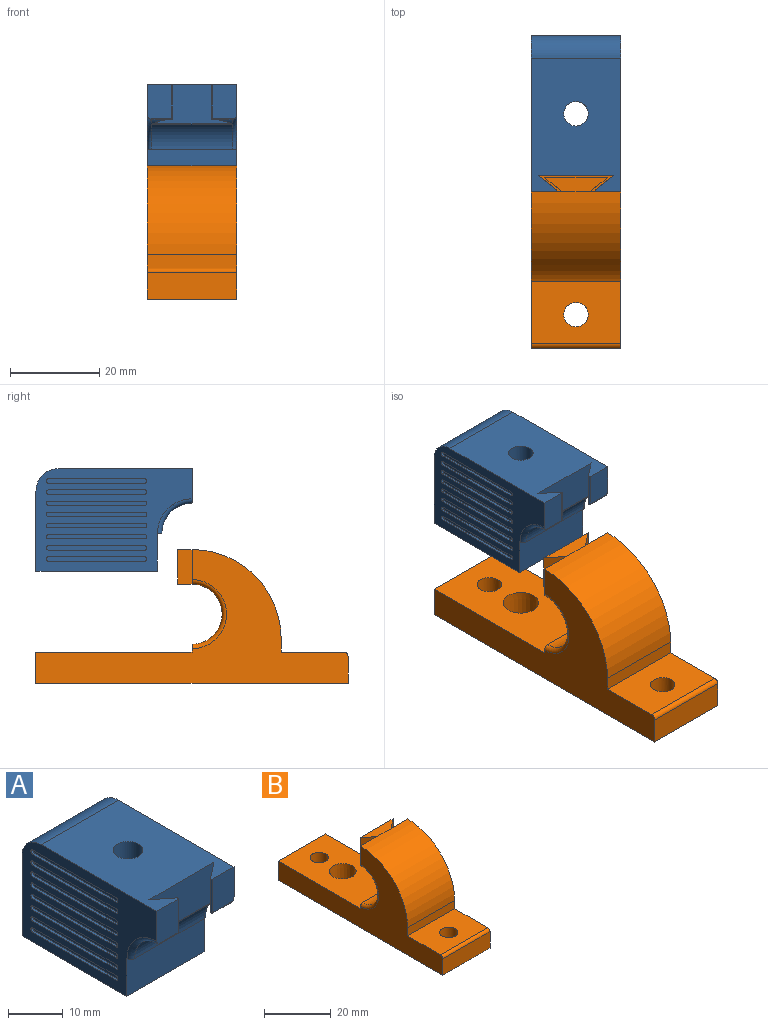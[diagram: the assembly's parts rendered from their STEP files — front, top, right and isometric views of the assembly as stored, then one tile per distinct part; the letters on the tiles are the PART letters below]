
ASSEMBLY  parts=2 mates=1
PART A: 114 faces, bbox 20.1x35.1x23.1 mm
  f0: cylinder r=6.75mm len=18mm, axis (1,0,0), area 119mm2, adj f5,f6,f15,f31
  f1: cylinder r=6.75mm len=4.48mm, axis (1,0,0), area 8.1mm2, adj f5,f24,f33
  f2: plane 7.5x5.48mm, normal (0,-1,0), area 41mm2, adj f4,f5,f7,f24,f25
  f3: cylinder r=6.75mm len=4.48mm, axis (1,0,0), area 8.1mm2, adj f6,f22,f26
  f4: plane 30x20mm, normal (0,0,1), area 531.4mm2, adj f2,f7,f10,f11,f16,f17,f18,f19
  f5: torus R=7.75mm, axis (-1,0,0), area 17.5mm2, adj f0,f1,f2,f7,f15,f24,f29,f32
  f6: torus R=7.75mm, axis (-1,0,0), area 17.5mm2, adj f0,f3,f10,f11,f15,f22,f27,f28
  f7: plane 35x23mm, normal (-1,0,0), area 507.5mm2, adj f2,f4,f5,f8,f9,f14,f15,f20
  f8: plane 27.22x20mm, normal (0,0,-1), area 407.5mm2, adj f7,f9,f10,f12,f14,f19
  f9: plane 20x18mm, normal (0,1,0), area 360mm2, adj f7,f8,f10,f20
  f10: plane 35x23mm, normal (1,0,0), area 507.5mm2, adj f4,f6,f8,f9,f11,f14,f15,f20
  f11: plane 7.5x5.48mm, normal (0,-1,0), area 41mm2, adj f4,f6,f10,f21,f22
  f12: cylinder r=6mm len=12mm, axis (0,0,-1), area 377mm2, adj f8,f13
  f13: cone r=0mm half-angle=59deg, axis (0,0,-1), area 131.9mm2, adj f12
  f14: plane 20x8.5mm, normal (0,-1,0), area 170mm2, adj f7,f8,f10,f15
  f15: plane 20x1.03mm, normal (0,0,-1), area 20.2mm2, adj f0,f5,f6,f7,f10,f14
  f16: plane 8.41x4.06mm, normal (0.62,0.79,0), area 40.5mm2, adj f4,f18,f25,f33
  f17: plane 8.41x4.06mm, normal (-0.62,0.79,0), area 40.5mm2, adj f4,f18,f21,f26
  f18: plane 17.29x8.75mm, normal (0,-1,0), area 146.5mm2, adj f4,f16,f17,f26,f31,f33
  f19: cylinder r=2.75mm len=23mm, axis (0,0,-1), area 397.4mm2, adj f4,f8
  f20: cylinder r=5mm len=20mm, axis (1,0,0), area 157.1mm2, adj f4,f7,f9,f10
  f21: cylinder r=0.25mm len=7.5mm, axis (0,0,-1), area 4.6mm2, adj f4,f11,f17,f23
  f22: cylinder r=0.25mm len=5.14mm, axis (1,0,0), area 1.8mm2, adj f3,f6,f11,f23
  f23: sphere r=0.25mm, area 0.2mm2, adj f21,f22,f26
  f24: cylinder r=0.25mm len=5.14mm, axis (1,0,0), area 1.8mm2, adj f1,f2,f5,f30
  f25: cylinder r=0.25mm len=7.5mm, axis (0,0,1), area 4.6mm2, adj f2,f4,f16,f30
  f26: bspline ~4.64x3.74mm, area 2.5mm2, adj f3,f17,f18,f23,f27,f31
  f27: bspline ~0.95x0.81mm, area 0mm2, adj f6,f26,f28,f31
  f28: bspline ~0.43x0.25mm, area 0mm2, adj f6,f27,f31
  f29: bspline ~0.43x0.25mm, area 0mm2, adj f5,f31,f32
  f30: sphere r=0.25mm, area 0.2mm2, adj f24,f25,f33
  f31: cylinder r=0.25mm len=18mm, axis (1,0,0), area 4.3mm2, adj f0,f18,f26,f27,f28,f29,f32,f33
  f32: bspline ~0.95x0.81mm, area 0mm2, adj f5,f29,f31,f33
  f33: bspline ~4.64x3.74mm, area 2.5mm2, adj f1,f16,f18,f30,f31,f32
  f34: cylinder r=0.5mm len=1mm, axis (1,0,0), area 0.8mm2, adj f10,f35,f37,f38
  f35: plane 21.56x0.5mm, normal (0,0,1), area 10.8mm2, adj f10,f34,f36,f38
  f36: cylinder r=0.5mm len=1mm, axis (1,0,0), area 0.8mm2, adj f10,f35,f37,f38
  f37: plane 21.56x0.5mm, normal (0,0,-1), area 10.8mm2, adj f10,f34,f36,f38
  f38: plane 22.56x1mm, normal (1,0,0), area 22.3mm2, adj f34,f35,f36,f37
  f39: cylinder r=0.5mm len=1mm, axis (1,0,0), area 0.8mm2, adj f10,f40,f42,f43
  f40: plane 21.56x0.5mm, normal (0,0,1), area 10.8mm2, adj f10,f39,f41,f43
  f41: cylinder r=0.5mm len=1mm, axis (1,0,0), area 0.8mm2, adj f10,f40,f42,f43
  f42: plane 21.56x0.5mm, normal (0,0,-1), area 10.8mm2, adj f10,f39,f41,f43
  f43: plane 22.56x1mm, normal (1,0,0), area 22.3mm2, adj f39,f40,f41,f42
  f44: cylinder r=0.5mm len=1mm, axis (1,0,0), area 0.8mm2, adj f10,f45,f47,f48
  f45: plane 21.56x0.5mm, normal (0,0,1), area 10.8mm2, adj f10,f44,f46,f48
  f46: cylinder r=0.5mm len=1mm, axis (1,0,0), area 0.8mm2, adj f10,f45,f47,f48
  f47: plane 21.56x0.5mm, normal (0,0,-1), area 10.8mm2, adj f10,f44,f46,f48
  f48: plane 22.56x1mm, normal (1,0,0), area 22.3mm2, adj f44,f45,f46,f47
  f49: cylinder r=0.5mm len=1mm, axis (1,0,0), area 0.8mm2, adj f10,f50,f52,f53
  f50: plane 21.56x0.5mm, normal (0,0,1), area 10.8mm2, adj f10,f49,f51,f53
  f51: cylinder r=0.5mm len=1mm, axis (1,0,0), area 0.8mm2, adj f10,f50,f52,f53
  f52: plane 21.56x0.5mm, normal (0,0,-1), area 10.8mm2, adj f10,f49,f51,f53
  f53: plane 22.56x1mm, normal (1,0,0), area 22.3mm2, adj f49,f50,f51,f52
  f54: cylinder r=0.5mm len=1mm, axis (1,0,0), area 0.8mm2, adj f10,f55,f57,f58
  f55: plane 21.56x0.5mm, normal (0,0,1), area 10.8mm2, adj f10,f54,f56,f58
  f56: cylinder r=0.5mm len=1mm, axis (1,0,0), area 0.8mm2, adj f10,f55,f57,f58
  f57: plane 21.56x0.5mm, normal (0,0,-1), area 10.8mm2, adj f10,f54,f56,f58
  f58: plane 22.56x1mm, normal (1,0,0), area 22.3mm2, adj f54,f55,f56,f57
  f59: cylinder r=0.5mm len=1mm, axis (1,0,0), area 0.8mm2, adj f10,f60,f62,f63
  f60: plane 21.56x0.5mm, normal (0,0,1), area 10.8mm2, adj f10,f59,f61,f63
  f61: cylinder r=0.5mm len=1mm, axis (1,0,0), area 0.8mm2, adj f10,f60,f62,f63
  f62: plane 21.56x0.5mm, normal (0,0,-1), area 10.8mm2, adj f10,f59,f61,f63
  f63: plane 22.56x1mm, normal (1,0,0), area 22.3mm2, adj f59,f60,f61,f62
  f64: cylinder r=0.5mm len=1mm, axis (1,0,0), area 0.8mm2, adj f10,f65,f67,f68
  f65: plane 21.56x0.5mm, normal (0,0,1), area 10.8mm2, adj f10,f64,f66,f68
  f66: cylinder r=0.5mm len=1mm, axis (1,0,0), area 0.8mm2, adj f10,f65,f67,f68
  f67: plane 21.56x0.5mm, normal (0,0,-1), area 10.8mm2, adj f10,f64,f66,f68
  f68: plane 22.56x1mm, normal (1,0,0), area 22.3mm2, adj f64,f65,f66,f67
  f69: cylinder r=0.5mm len=1mm, axis (1,0,0), area 0.8mm2, adj f10,f70,f72,f73
  f70: plane 21.56x0.5mm, normal (0,0,1), area 10.8mm2, adj f10,f69,f71,f73
  f71: cylinder r=0.5mm len=1mm, axis (1,0,0), area 0.8mm2, adj f10,f70,f72,f73
  f72: plane 21.56x0.5mm, normal (0,0,-1), area 10.8mm2, adj f10,f69,f71,f73
  f73: plane 22.56x1mm, normal (1,0,0), area 22.3mm2, adj f69,f70,f71,f72
  f74: plane 21.56x0.5mm, normal (0,0,1), area 10.8mm2, adj f7,f75,f77,f78
  f75: cylinder r=0.5mm len=1mm, axis (-1,0,0), area 0.8mm2, adj f7,f74,f76,f78
  f76: plane 21.56x0.5mm, normal (0,0,-1), area 10.8mm2, adj f7,f75,f77,f78
  f77: cylinder r=0.5mm len=1mm, axis (-1,0,0), area 0.8mm2, adj f7,f74,f76,f78
  f78: plane 22.56x1mm, normal (-1,0,0), area 22.3mm2, adj f74,f75,f76,f77
  f79: plane 21.56x0.5mm, normal (0,0,1), area 10.8mm2, adj f7,f80,f82,f83
  f80: cylinder r=0.5mm len=1mm, axis (-1,0,0), area 0.8mm2, adj f7,f79,f81,f83
  f81: plane 21.56x0.5mm, normal (0,0,-1), area 10.8mm2, adj f7,f80,f82,f83
  f82: cylinder r=0.5mm len=1mm, axis (-1,0,0), area 0.8mm2, adj f7,f79,f81,f83
  f83: plane 22.56x1mm, normal (-1,0,0), area 22.3mm2, adj f79,f80,f81,f82
  f84: plane 21.56x0.5mm, normal (0,0,1), area 10.8mm2, adj f7,f85,f87,f88
  f85: cylinder r=0.5mm len=1mm, axis (-1,0,0), area 0.8mm2, adj f7,f84,f86,f88
  f86: plane 21.56x0.5mm, normal (0,0,-1), area 10.8mm2, adj f7,f85,f87,f88
  f87: cylinder r=0.5mm len=1mm, axis (-1,0,0), area 0.8mm2, adj f7,f84,f86,f88
  f88: plane 22.56x1mm, normal (-1,0,0), area 22.3mm2, adj f84,f85,f86,f87
  f89: plane 21.56x0.5mm, normal (0,0,1), area 10.8mm2, adj f7,f90,f92,f93
  f90: cylinder r=0.5mm len=1mm, axis (-1,0,0), area 0.8mm2, adj f7,f89,f91,f93
  f91: plane 21.56x0.5mm, normal (0,0,-1), area 10.8mm2, adj f7,f90,f92,f93
  f92: cylinder r=0.5mm len=1mm, axis (-1,0,0), area 0.8mm2, adj f7,f89,f91,f93
  f93: plane 22.56x1mm, normal (-1,0,0), area 22.3mm2, adj f89,f90,f91,f92
  f94: plane 21.56x0.5mm, normal (0,0,1), area 10.8mm2, adj f7,f95,f97,f98
  f95: cylinder r=0.5mm len=1mm, axis (-1,0,0), area 0.8mm2, adj f7,f94,f96,f98
  f96: plane 21.56x0.5mm, normal (0,0,-1), area 10.8mm2, adj f7,f95,f97,f98
  f97: cylinder r=0.5mm len=1mm, axis (-1,0,0), area 0.8mm2, adj f7,f94,f96,f98
  f98: plane 22.56x1mm, normal (-1,0,0), area 22.3mm2, adj f94,f95,f96,f97
  f99: plane 21.56x0.5mm, normal (0,0,1), area 10.8mm2, adj f7,f100,f102,f103
  f100: cylinder r=0.5mm len=1mm, axis (-1,0,0), area 0.8mm2, adj f7,f99,f101,f103
  f101: plane 21.56x0.5mm, normal (0,0,-1), area 10.8mm2, adj f7,f100,f102,f103
  f102: cylinder r=0.5mm len=1mm, axis (-1,0,0), area 0.8mm2, adj f7,f99,f101,f103
  f103: plane 22.56x1mm, normal (-1,0,0), area 22.3mm2, adj f99,f100,f101,f102
  f104: plane 21.56x0.5mm, normal (0,0,1), area 10.8mm2, adj f7,f105,f107,f108
  f105: cylinder r=0.5mm len=1mm, axis (-1,0,0), area 0.8mm2, adj f7,f104,f106,f108
  f106: plane 21.56x0.5mm, normal (0,0,-1), area 10.8mm2, adj f7,f105,f107,f108
  f107: cylinder r=0.5mm len=1mm, axis (-1,0,0), area 0.8mm2, adj f7,f104,f106,f108
  f108: plane 22.56x1mm, normal (-1,0,0), area 22.3mm2, adj f104,f105,f106,f107
  f109: plane 21.56x0.5mm, normal (0,0,1), area 10.8mm2, adj f7,f110,f112,f113
  f110: cylinder r=0.5mm len=1mm, axis (-1,0,0), area 0.8mm2, adj f7,f109,f111,f113
  f111: plane 21.56x0.5mm, normal (0,0,-1), area 10.8mm2, adj f7,f110,f112,f113
  f112: cylinder r=0.5mm len=1mm, axis (-1,0,0), area 0.8mm2, adj f7,f109,f111,f113
  f113: plane 22.56x1mm, normal (-1,0,0), area 22.3mm2, adj f109,f110,f111,f112
PART B: 26 faces, bbox 20x70x30 mm
  f0: cylinder r=6.75mm len=18mm, axis (1,0,0), area 381.7mm2, adj f16,f17,f18,f20,f21,f24
  f1: plane 14x7.75mm, normal (0,1,0), area 108.5mm2, adj f2,f3,f11,f24
  f2: plane 7.75x4mm, normal (0.62,-0.79,0), area 39.5mm2, adj f1,f11,f21,f24
  f3: plane 7.75x4mm, normal (-0.62,-0.79,0), area 39.5mm2, adj f1,f11,f20,f24
  f4: plane 70x30mm, normal (-1,0,0), area 769.6mm2, adj f6,f7,f8,f9,f10,f12,f13,f16
  f5: plane 70x30mm, normal (1,0,0), area 769.6mm2, adj f6,f7,f8,f9,f10,f12,f13,f17
  f6: plane 20x7mm, normal (0,1,0), area 140mm2, adj f4,f5,f9,f19
  f7: plane 20x6mm, normal (0,-1,0), area 120mm2, adj f4,f5,f9,f12
  f8: plane 20x14mm, normal (0,0,1), area 256.2mm2, adj f4,f5,f10,f12,f14
  f9: plane 70x20mm, normal (0,0,-1), area 1305.7mm2, adj f4,f5,f6,f7,f14,f15,f25
  f10: plane 20x3mm, normal (0,-1,0), area 60mm2, adj f4,f5,f8,f13
  f11: plane 14x3.16mm, normal (0,0,1), area 31.6mm2, adj f1,f2,f3,f13
  f12: cylinder r=1mm len=20mm, axis (-1,0,0), area 31.4mm2, adj f4,f5,f7,f8
  f13: cylinder r=20mm len=20mm, axis (-1,0,0), area 628.3mm2, adj f4,f5,f10,f11,f20,f21
  f14: cylinder r=2.75mm len=7mm, axis (0,0,-1), area 121mm2, adj f8,f9
  f15: cylinder r=2.75mm len=7mm, axis (0,0,-1), area 121mm2, adj f9,f19
  f16: torus R=7.75mm, axis (-1,0,0), area 35.1mm2, adj f0,f4,f18,f20
  f17: torus R=7.75mm, axis (-1,0,0), area 35.1mm2, adj f0,f5,f18,f21
  f18: plane 20x1.75mm, normal (0,1,0), area 34.6mm2, adj f0,f4,f5,f16,f17,f19
  f19: plane 35x20mm, normal (0,0,1), area 626mm2, adj f4,f5,f6,f15,f18,f22
  f20: plane 7.75x7mm, normal (0,1,0), area 54mm2, adj f0,f3,f4,f13,f16
  f21: plane 7.75x7mm, normal (0,1,0), area 54mm2, adj f0,f2,f5,f13,f17
  f22: cone r=4mm half-angle=1.2deg, axis (0,0,1), area 165.5mm2, adj f19,f23
  f23: plane 7.72x7.72mm, normal (0,0,1), area 0mm2, adj f22,f25
  f24: plane 14x3.16mm, normal (0,0,-1), area 31.6mm2, adj f0,f1,f2,f3
  f25: cylinder r=3.86mm len=7.72mm, axis (0,0,1), area 7.3mm2, adj f9,f23
PLACE A t=(-9.36,11.22,20.61)mm
PLACE B t=(-9.36,11.22,2.48)mm
MATE slider A.f4 <-> B.f11  axis (0,0,1) through (0.64,11.22,50.61)mm
